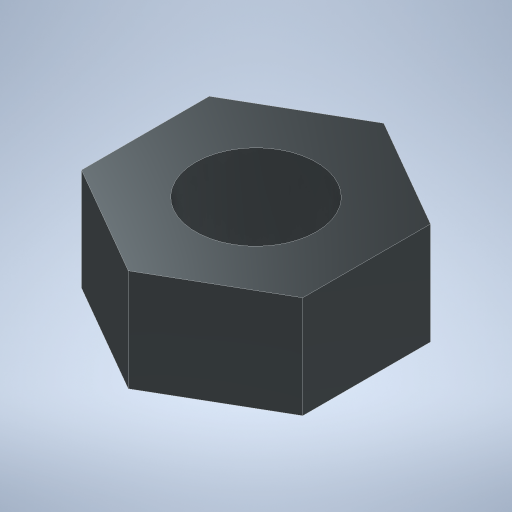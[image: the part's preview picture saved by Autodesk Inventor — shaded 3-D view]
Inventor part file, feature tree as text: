
AUTODESK INVENTOR PART (.ipt)
format: ipt  version: 2024 (Build 280153000, 153)  size: 212,480 bytes
history: native  units: in
note: dims shown in document units (in); Inventor stores cm internally (conversion verified against a paired STEP export)
features: extrude x1, sketch x1
ambient origin geometry x8: Origin, YZ Plane, XZ Plane, XY Plane, X Axis, Y Axis, Z Axis, Center Point
bodies: Solid1 (feature_tree)
feature tree (2):
  extrude  "Extrusion1"  Depth=0.1in
  sketch  "Sketch1"  dims[d0=0.1083in d1=0.1181in d2=0.1in d3=0.0in]
